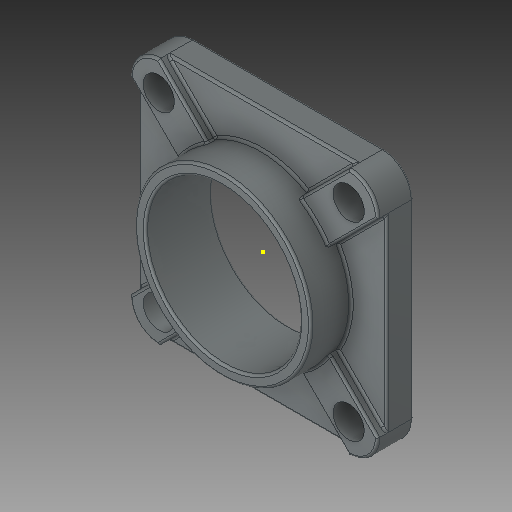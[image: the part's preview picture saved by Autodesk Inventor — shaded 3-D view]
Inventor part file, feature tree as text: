
AUTODESK INVENTOR PART (.ipt)
format: ipt  version: 2019 (Build 230136000, 136)  size: 485,888 bytes
history: native  units: in
note: dims shown in document units (in); Inventor stores cm internally (conversion verified against a paired STEP export)
features: sketch x10, other x3
ambient origin geometry x8: Origin, YZ Plane, XZ Plane, XY Plane, X Axis, Y Axis, Z Axis, Center Point
bodies: Solid1 (feature_tree)
feature tree (13):
  other  "project flange bearing part1_MIR7.ipt"
  other  "Solid1::project flange bearing part1_MIR7.ipt"
  other  "TaggingFeature1"
  sketch  "Sketch1"  dims[d0=0.3937in]
  sketch  "Sketch2"
  sketch  "Sketch3"
  sketch  "Sketch4"
  sketch  "Sketch5"
  sketch  "Sketch6"
  sketch  "Sketch7"
  sketch  "Sketch8"
  sketch  "Sketch9"
  sketch  "Sketch10"
